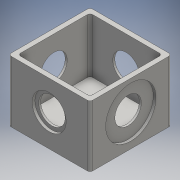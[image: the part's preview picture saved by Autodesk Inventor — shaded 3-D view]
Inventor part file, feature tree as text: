
AUTODESK INVENTOR PART (.ipt)
format: ipt  version: 2016 (Build 200138000, 138)  size: 167,424 bytes
history: native  units: mm
features: extrude x5, sketch x5, mirror x2, pattern_circular x1
ambient origin geometry x8: Origin, YZ Plane, XZ Plane, XY Plane, X Axis, Y Axis, Z Axis, Center Point
bodies: Solid1 (feature_tree)
feature tree (13):
  extrude  "Extrusion1"  Depth=60.0mm
  extrude  "Extrusion2"  Depth=30.0mm
  extrude  "Extrusion3"  Depth=45.0mm TaperAngle=0.0deg
  mirror  "Mirror1"
  extrude  "Extrusion4"  Depth=53.0mm
  mirror  "Mirror2"
  extrude  "Extrusion5"  Depth=40.0mm
  pattern_circular  "Circular Pattern1"  [2 undecoded]
  sketch  "Sketch1"  dims[d0=60.0mm d1=60.0mm]
  sketch  "Sketch2"  dims[d2=30.0mm d3=30.0mm]
  sketch  "Sketch3"  dims[d4=2.0mm d5=45.0mm d6=0.0mm]
  sketch  "Sketch4"  dims[d7=53.0mm d8=53.0mm]
  sketch  "Sketch5"  dims[d9=26.5mm d10=26.5mm d11=2.0mm d12=40.0mm d13=0.0mm d14=37.0mm d15=23.5mm d16=2.0mm d17=0.0mm d18=25.0mm d19=23.5mm d20=2.0mm d21=0.0mm d22=19.5mm d23=2.0mm d24=0.0mm d25=40.0mm d26=360.0deg]
note: 2 required parameter values undecoded (feature->parameter linkage not recoverable at this tier; creation-order binding heuristic only, values carry confidence <= 0.55)
